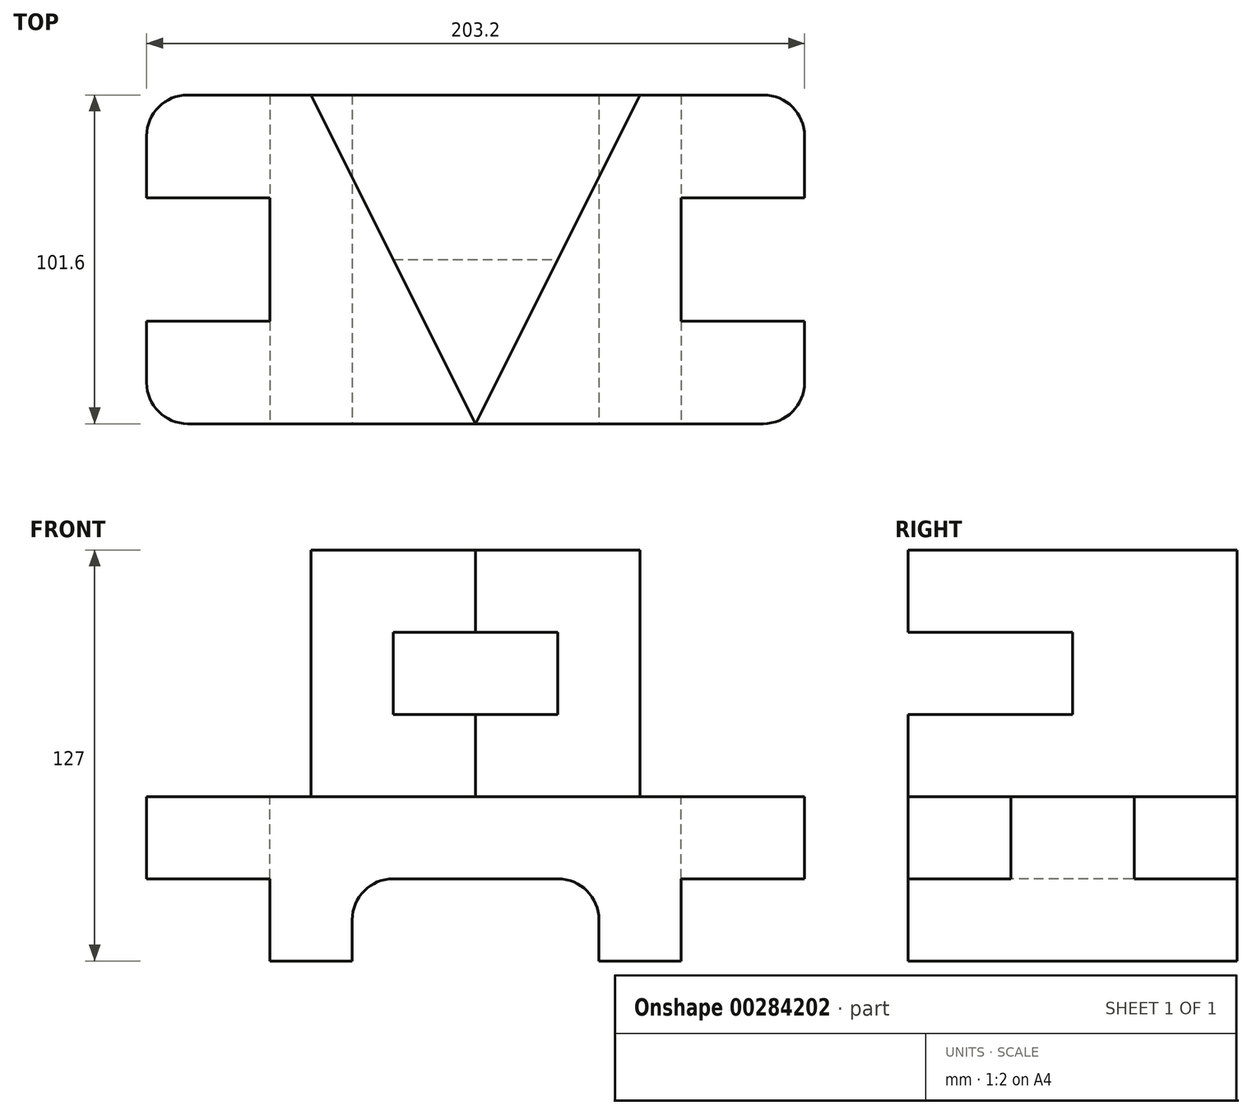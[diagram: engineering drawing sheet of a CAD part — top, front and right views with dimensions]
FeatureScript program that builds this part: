
annotation { "Feature Type Name" : "Feature", "Feature Type Description" : "" }
export const myFeature = defineFeature(function(context is Context, id is Id, definition is map)
    precondition{}
    {
        {
            var Q0;
            Q0=qCreatedBy(makeId("Front.planeOp"),FACE);
            var sketch = newSketch(context, id + "F0", { "sketchPlane" : qUnion([Q0])});
            skLineSegment(sketch, "E0", {"start": v(0, 0) * mm, "end": v(203.2, 0) * mm});
            skLineSegment(sketch, "E1", {"start": v(0, 0) * mm, "end": v(0, 127) * mm});
            skLineSegment(sketch, "E2", {"start": v(0, 127) * mm, "end": v(203.2, 127) * mm});
            skLineSegment(sketch, "E3", {"start": v(203.2, 127) * mm, "end": v(203.2, 0) * mm});
            skSolve(sketch);
        }
        {
            var Q0;
            Q0=makeQuery(id+"F0.imprint","IMPRINT",FACE,{"disambiguationData":[TD([[makeQuery(id+"F0.imprint","IMPRINT",EDGE,{"derivedFrom":sQuery(id+"F0.wireOp",EDGE,"E0")}),1.0]])]});
            extrude(context, id + "F1", {"entities" : qUnion([Q0]), "depth" : 101.6 * mm});
        }
        {
            var Q0;
            Q0=makeQuery(id+"F1.opExtrude","CAP_EDGE",EDGE,{"disambiguationData":[OSD([sQuery(id+"F0.wireOp",EDGE,"E1")])],"isStart":true});
            var Q1;
            Q1=makeQuery(id+"F1.opExtrude","CAP_EDGE",EDGE,{"disambiguationData":[OSD([sQuery(id+"F0.wireOp",EDGE,"E1")])],"isStart":false});
            var Q2;
            Q2=makeQuery(id+"F1.opExtrude","CAP_EDGE",EDGE,{"disambiguationData":[OSD([sQuery(id+"F0.wireOp",EDGE,"E3")])],"isStart":false});
            var Q3;
            Q3=makeQuery(id+"F1.opExtrude","CAP_EDGE",EDGE,{"disambiguationData":[OSD([sQuery(id+"F0.wireOp",EDGE,"E3")])],"isStart":true});
            fillet(context, id + "F2", {"entities" : qUnion([Q0, Q1, Q2, Q3]), "radius" : 12.7 * mm, "tangentPropagation" : true, "allowEdgeOverflow" : false});
        }
        {
            var Q0;
            Q0=makeQuery(id+"F1.opExtrude","CAP_FACE",FACE,{"disambiguationData":[OSD([sQuery(id+"F0.wireOp",EDGE,"E0"),sQuery(id+"F0.wireOp",EDGE,"E1"),sQuery(id+"F0.wireOp",EDGE,"E2"),sQuery(id+"F0.wireOp",EDGE,"E3")])],"isStart":false});
            var sketch = newSketch(context, id + "F3", { "sketchPlane" : qUnion([Q0])});
            skLineSegment(sketch, "E4", {"start": v(0, 0) * mm, "end": v(38.1, 0) * mm});
            skLineSegment(sketch, "E5", {"start": v(38.1, 0) * mm, "end": v(38.1, 25.4) * mm});
            skLineSegment(sketch, "E6", {"start": v(38.1, 25.4) * mm, "end": v(0, 25.4) * mm});
            skLineSegment(sketch, "E7", {"start": v(0, 25.4) * mm, "end": v(0, 0) * mm});
            skLineSegment(sketch, "E8", {"start": v(203.2, 0) * mm, "end": v(203.2, 25.4) * mm});
            skLineSegment(sketch, "E9", {"start": v(203.2, 25.4) * mm, "end": v(165.1, 25.4) * mm});
            skLineSegment(sketch, "E10", {"start": v(165.1, 25.4) * mm, "end": v(165.1, 0) * mm});
            skLineSegment(sketch, "E11", {"start": v(165.1, 0) * mm, "end": v(203.2, 0) * mm});
            skSolve(sketch);
        }
        {
            var Q0;
            {var subQ4=sQuery(id+"F3.wireOp",EDGE,"E7");Q0=makeQuery(id+"F3.imprint","IMPRINT",FACE,{"disambiguationData":[TD([[makeQuery(id+"F3.imprint","IMPRINT",EDGE,{"derivedFrom":subQ4}),1.0]])]});}
            var Q1;
            {var subQ5=sQuery(id+"F3.wireOp",EDGE,"E5");Q1=makeQuery(id+"F3.imprint","IMPRINT",FACE,{"disambiguationData":[TD([[makeQuery(id+"F3.imprint","IMPRINT",EDGE,{"derivedFrom":subQ5}),1.0]])]});}
            var Q2;
            {var subQ0=sQuery(id+"F3.wireOp",EDGE,"E10");Q2=makeQuery(id+"F3.imprint","IMPRINT",FACE,{"disambiguationData":[TD([[makeQuery(id+"F3.imprint","IMPRINT",EDGE,{"derivedFrom":subQ0}),1.0]])]});}
            var Q3;
            {var subQ0=sQuery(id+"F3.wireOp",EDGE,"E8");Q3=makeQuery(id+"F3.imprint","IMPRINT",FACE,{"disambiguationData":[TD([[makeQuery(id+"F3.imprint","IMPRINT",EDGE,{"derivedFrom":subQ0}),1.0]])]});}
            extrude(context, id + "F4", {"entities" : qUnion([Q0, Q1, Q2, Q3]), "operationType" : NewBodyOperationType.REMOVE, "endBound" : BoundingType.THROUGH_ALL, "oppositeDirection" : true, "depth" : 25.4 * mm});
        }
        {
            var Q0;
            Q0=makeQuery(id+"F1.opExtrude","SWEPT_FACE",FACE,{"disambiguationData":[OSD([sQuery(id+"F0.wireOp",EDGE,"E2")])]});
            var sketch = newSketch(context, id + "F5", { "sketchPlane" : qUnion([Q0])});
            skLineSegment(sketch, "E12", {"start": v(0, -50.8) * mm, "end": v(38.1, -50.8) * mm});
            skLineSegment(sketch, "E13", {"start": v(38.1, -50.8) * mm, "end": v(38.1, -31.75) * mm});
            skLineSegment(sketch, "E14", {"start": v(38.1, -31.75) * mm, "end": v(0, -31.75) * mm});
            skLineSegment(sketch, "E15", {"start": v(0, -31.75) * mm, "end": v(0, -50.8) * mm});
            skLineSegment(sketch, "E16.MirrorCS", {"start": v(38.1, -69.85) * mm, "end": v(0, -69.85) * mm});
            skLineSegment(sketch, "E17.MirrorCS", {"start": v(38.1, -50.8) * mm, "end": v(38.1, -69.85) * mm});
            skLineSegment(sketch, "E18.MirrorCS", {"start": v(0, -69.85) * mm, "end": v(0, -50.8) * mm});
            skLineSegment(sketch, "E19", {"start": v(203.2, -50.8) * mm, "end": v(203.2, -31.75) * mm});
            skLineSegment(sketch, "E20", {"start": v(203.2, -31.75) * mm, "end": v(165.1, -31.75) * mm});
            skLineSegment(sketch, "E21", {"start": v(165.1, -31.75) * mm, "end": v(165.1, -50.8) * mm});
            skLineSegment(sketch, "E22", {"start": v(165.1, -50.8) * mm, "end": v(203.2, -50.8) * mm});
            skLineSegment(sketch, "E23.MirrorCS", {"start": v(203.2, -69.85) * mm, "end": v(165.1, -69.85) * mm});
            skLineSegment(sketch, "E24.MirrorCS", {"start": v(165.1, -69.85) * mm, "end": v(165.1, -50.8) * mm});
            skLineSegment(sketch, "E25.MirrorCS", {"start": v(203.2, -50.8) * mm, "end": v(203.2, -69.85) * mm});
            skSolve(sketch);
        }
        {
            var Q0;
            Q0=makeQuery(id+"F5.imprint","IMPRINT",FACE,{"disambiguationData":[TD([[makeQuery(id+"F5.imprint","IMPRINT",EDGE,{"derivedFrom":sQuery(id+"F5.wireOp",EDGE,"E19")}),1.0]])]});
            var Q1;
            Q1=makeQuery(id+"F5.imprint","IMPRINT",FACE,{"disambiguationData":[TD([[makeQuery(id+"F5.imprint","IMPRINT",EDGE,{"derivedFrom":sQuery(id+"F5.wireOp",EDGE,"E22")}),-1.0]])]});
            var Q2;
            Q2=makeQuery(id+"F5.imprint","IMPRINT",FACE,{"disambiguationData":[TD([[makeQuery(id+"F5.imprint","IMPRINT",EDGE,{"derivedFrom":sQuery(id+"F5.wireOp",EDGE,"E12")}),1.0]])]});
            var Q3;
            Q3=makeQuery(id+"F5.imprint","IMPRINT",FACE,{"disambiguationData":[TD([[makeQuery(id+"F5.imprint","IMPRINT",EDGE,{"derivedFrom":sQuery(id+"F5.wireOp",EDGE,"E12")}),-1.0]])]});
            extrude(context, id + "F6", {"entities" : qUnion([Q0, Q1, Q2, Q3]), "operationType" : NewBodyOperationType.REMOVE, "endBound" : BoundingType.THROUGH_ALL, "oppositeDirection" : true, "depth" : 25.4 * mm});
        }
        {
            var Q0;
            Q0=makeQuery(id+"F1.opExtrude","SWEPT_FACE",FACE,{"disambiguationData":[OSD([sQuery(id+"F0.wireOp",EDGE,"E2")])]});
            var sketch = newSketch(context, id + "F7", { "sketchPlane" : qUnion([Q0])});
            skLineSegment(sketch, "E26", {"start": v(101.6, 0) * mm, "end": v(152.4, 0) * mm});
            skLineSegment(sketch, "E27", {"start": v(152.4, 0) * mm, "end": v(101.6, -101.6) * mm});
            skLineSegment(sketch, "E28", {"start": v(101.6, -101.6) * mm, "end": v(101.6, 0) * mm});
            skLineSegment(sketch, "E29", {"start": v(101.6, 0) * mm, "end": v(50.8, 0) * mm});
            skLineSegment(sketch, "E30", {"start": v(50.8, 0) * mm, "end": v(101.6, -101.6) * mm});
            skLineSegment(sketch, "E31", {"start": v(101.6, 0) * mm, "end": v(101.6, -101.6) * mm});
            skSolve(sketch);
        }
        {
            var Q0;
            {var subQ10=sQuery(id+"F7.wireOp",EDGE,"E30");Q0=makeQuery(id+"F7.imprint","IMPRINT",FACE,{"disambiguationData":[TD([[makeQuery(id+"F7.imprint","IMPRINT",EDGE,{"derivedFrom":subQ10}),-1.0]])]});}
            var Q1;
            {var subQ6=sQuery(id+"F7.wireOp",EDGE,"E27");Q1=makeQuery(id+"F7.imprint","IMPRINT",FACE,{"disambiguationData":[TD([[makeQuery(id+"F7.imprint","IMPRINT",EDGE,{"derivedFrom":subQ6}),1.0]])]});}
            extrude(context, id + "F8", {"entities" : qUnion([Q0, Q1]), "operationType" : NewBodyOperationType.REMOVE, "oppositeDirection" : true, "depth" : 76.2 * mm});
        }
        {
            var Q0;
            Q0=makeQuery(id+"F1.opExtrude","CAP_FACE",FACE,{"disambiguationData":[OSD([sQuery(id+"F0.wireOp",EDGE,"E0"),sQuery(id+"F0.wireOp",EDGE,"E1"),sQuery(id+"F0.wireOp",EDGE,"E2"),sQuery(id+"F0.wireOp",EDGE,"E3")])],"isStart":false});
            var sketch = newSketch(context, id + "F9", { "sketchPlane" : qUnion([Q0])});
            skLineSegment(sketch, "E32", {"start": v(101.6, 0) * mm, "end": v(101.6, 25.4) * mm});
            skLineSegment(sketch, "E33", {"start": v(101.6, 25.4) * mm, "end": v(76.2, 25.4) * mm});
            skLineSegment(sketch, "E34", {"start": v(63.5, 12.7) * mm, "end": v(63.5, 0) * mm});
            skLineSegment(sketch, "E35", {"start": v(63.5, 0) * mm, "end": v(101.6, 0) * mm});
            skLineSegment(sketch, "E36.MirrorCS", {"start": v(101.6, 25.4) * mm, "end": v(127, 25.4) * mm});
            skLineSegment(sketch, "E37.MirrorCS", {"start": v(139.7, 12.7) * mm, "end": v(139.7, 0) * mm});
            skLineSegment(sketch, "E38.MirrorCS", {"start": v(139.7, 0) * mm, "end": v(101.6, 0) * mm});
            skPoint(sketch, "E39.visualSharp", {"position": v(63.5, 25.4) * mm});
            skArc(sketch, "E39.filletArc", {"start": v(76.2, 25.4) * mm, "mid": v(67.22, 21.68) * mm, "end": v(63.5, 12.7) * mm});
            skPoint(sketch, "E40.visualSharp", {"position": v(139.7, 25.4) * mm});
            skArc(sketch, "E40.filletArc", {"start": v(139.7, 12.7) * mm, "mid": v(135.98, 21.68) * mm, "end": v(127, 25.4) * mm});
            skSolve(sketch);
        }
        {
            var Q0;
            Q0=makeQuery(id+"F9.imprint","IMPRINT",FACE,{"disambiguationData":[TD([[makeQuery(id+"F9.imprint","IMPRINT",EDGE,{"derivedFrom":sQuery(id+"F9.wireOp",EDGE,"E32")}),1.0]])]});
            var Q1;
            Q1=makeQuery(id+"F9.imprint","IMPRINT",FACE,{"disambiguationData":[TD([[makeQuery(id+"F9.imprint","IMPRINT",EDGE,{"derivedFrom":sQuery(id+"F9.wireOp",EDGE,"E32")}),-1.0]])]});
            extrude(context, id + "F10", {"entities" : qUnion([Q0, Q1]), "operationType" : NewBodyOperationType.REMOVE, "endBound" : BoundingType.THROUGH_ALL, "oppositeDirection" : true, "depth" : 25.4 * mm});
        }
        {
            var Q0;
            Q0=makeQuery(id+"F1.opExtrude","SWEPT_FACE",FACE,{"disambiguationData":[OSD([sQuery(id+"F0.wireOp",EDGE,"E2")])]});
            var sketch = newSketch(context, id + "F11", { "sketchPlane" : qUnion([Q0])});
            skLineSegment(sketch, "E41", {"start": v(76.2, -50.8) * mm, "end": v(127, -50.8) * mm});
            skLineSegment(sketch, "E42", {"start": v(127, -50.8) * mm, "end": v(101.6, -101.6) * mm});
            skLineSegment(sketch, "E43", {"start": v(101.6, -101.6) * mm, "end": v(76.2, -50.8) * mm});
            skSolve(sketch);
        }
        {
            var Q0;
            Q0=makeQuery(id+"F11.imprint","IMPRINT",FACE,{"disambiguationData":[TD([[makeQuery(id+"F11.imprint","IMPRINT",EDGE,{"derivedFrom":sQuery(id+"F11.wireOp",EDGE,"E41")}),-1.0]])]});
            extrude(context, id + "F12", {"entities" : qUnion([Q0]), "operationType" : NewBodyOperationType.REMOVE, "oppositeDirection" : true, "depth" : 50.8 * mm, "hasSecondDirection" : true, "secondDirectionOppositeDirection" : true, "secondDirectionDepth" : 25.4 * mm});
        }
    });
